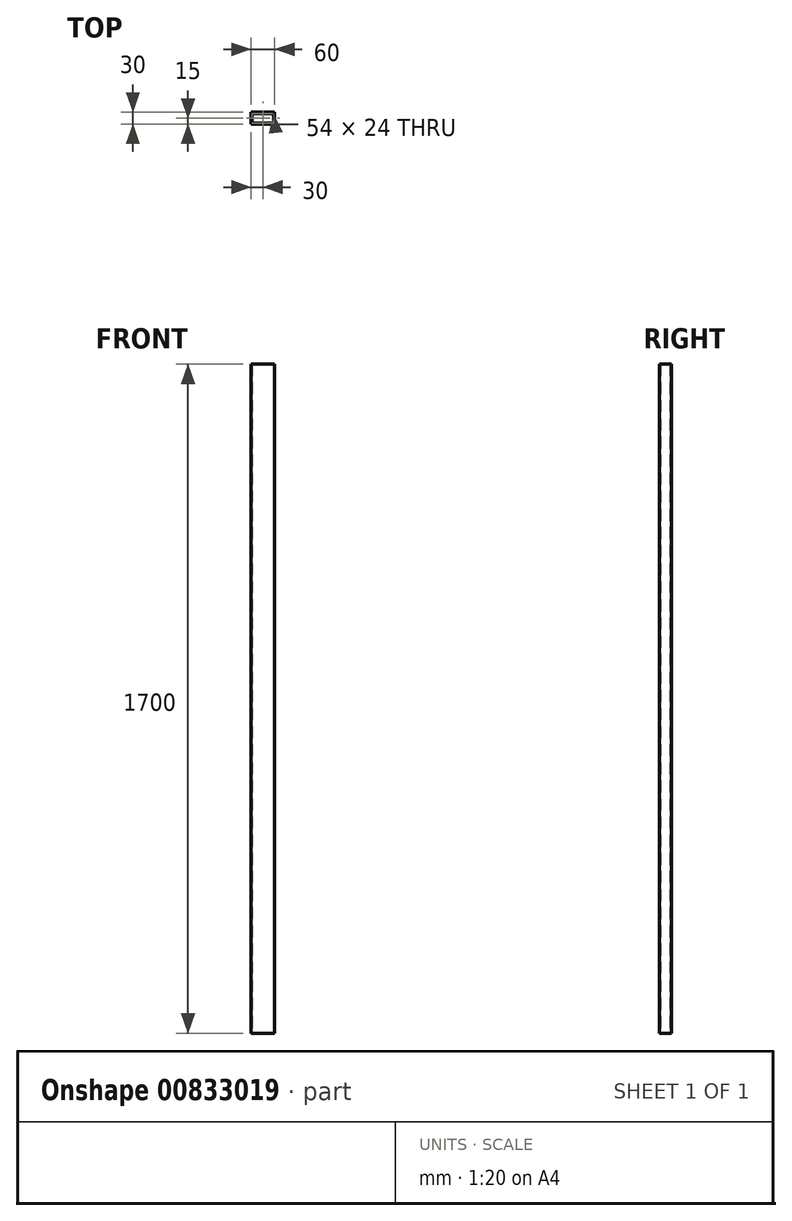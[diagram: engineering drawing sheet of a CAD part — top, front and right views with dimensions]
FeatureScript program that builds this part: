
annotation { "Feature Type Name" : "Feature", "Feature Type Description" : "" }
export const myFeature = defineFeature(function(context is Context, id is Id, definition is map)
    precondition{}
    {
        {
            var Q0;
            Q0=qCreatedBy(makeId("Top.planeOp"),FACE);
            var sketch = newSketch(context, id + "F0", { "sketchPlane" : qUnion([Q0])});
            skLineSegment(sketch, "E0.bottom", {"start": v(-30, 15) * mm, "end": v(30, 15) * mm});
            skLineSegment(sketch, "E0.top", {"start": v(-30, -15) * mm, "end": v(30, -15) * mm});
            skLineSegment(sketch, "E0.left", {"start": v(-30, 15) * mm, "end": v(-30, -15) * mm});
            skLineSegment(sketch, "E0.right", {"start": v(30, 15) * mm, "end": v(30, -15) * mm});
            skPoint(sketch, "E0.middle", {"position": v(0, 0) * mm});
            skLineSegment(sketch, "E1.bottom", {"start": v(-27, 12) * mm, "end": v(27, 12) * mm});
            skLineSegment(sketch, "E1.top", {"start": v(-27, -12) * mm, "end": v(27, -12) * mm});
            skLineSegment(sketch, "E1.left", {"start": v(-27, 12) * mm, "end": v(-27, -12) * mm});
            skLineSegment(sketch, "E1.right", {"start": v(27, 12) * mm, "end": v(27, -12) * mm});
            skSolve(sketch);
        }
        {
            var Q0;
            Q0=makeQuery(id+"F0.imprint","IMPRINT",FACE,{"disambiguationData":[TD([[makeQuery(id+"F0.imprint","IMPRINT",EDGE,{"derivedFrom":sQuery(id+"F0.wireOp",EDGE,"E0.bottom")}),-1.0]])]});
            extrude(context, id + "F1", {"entities" : qUnion([Q0]), "depth" : 1700 * mm, "offsetDistance" : 25 * mm});
        }
    });
